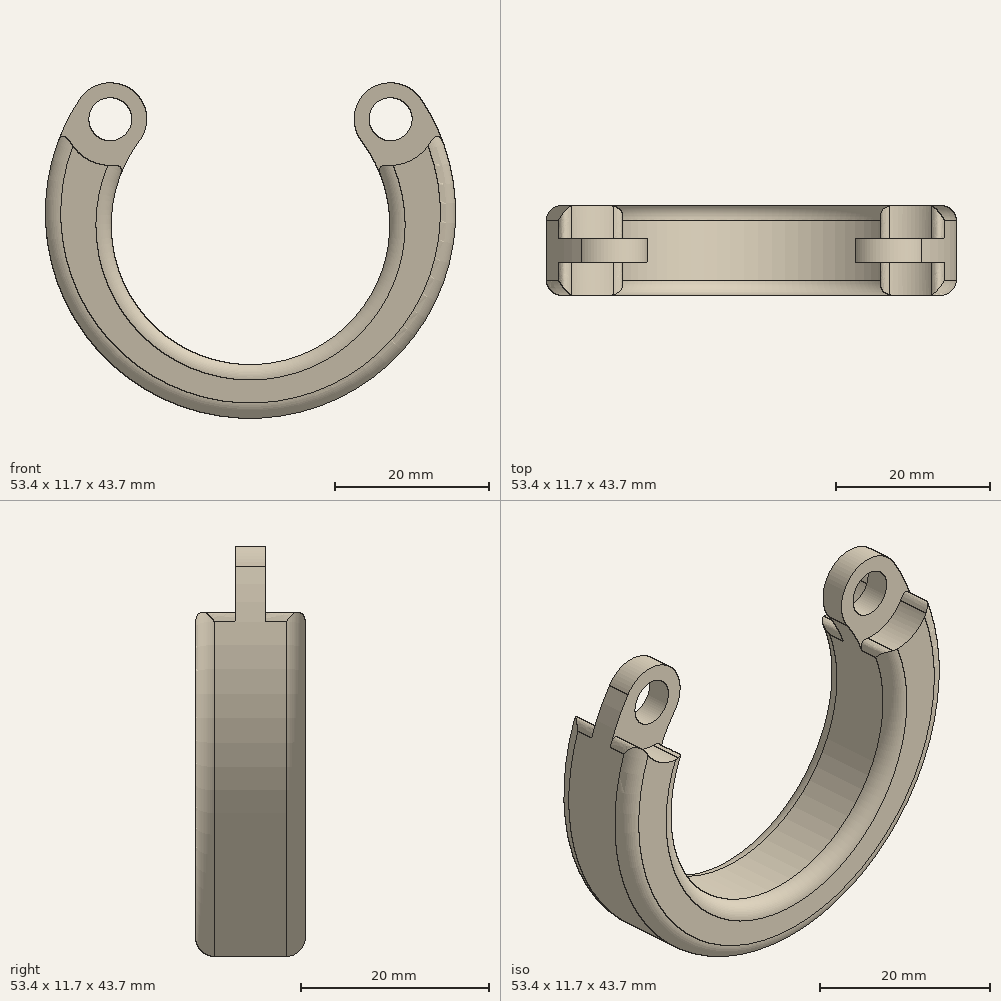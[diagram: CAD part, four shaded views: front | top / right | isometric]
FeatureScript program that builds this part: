
annotation { "Feature Type Name" : "Feature", "Feature Type Description" : "" }
export const myFeature = defineFeature(function(context is Context, id is Id, definition is map)
    precondition{}
    {
        {
            var Q0;
            Q0=qCreatedBy(makeId("Front.planeOp"),FACE);
            var sketch = newSketch(context, id + "F0", { "sketchPlane" : qUnion([Q0])});
            skLineSegment(sketch, "E0", {"start": v(-40.89, 0) * mm, "end": v(37.52, 0) * mm, "construction": true});
            skLineSegment(sketch, "E1", {"start": v(0, 27.57) * mm, "end": v(0, -28.48) * mm});
            skLineSegment(sketch, "E2", {"start": v(-18.25, 13.03) * mm, "end": v(18.25, 13.03) * mm, "construction": true});
            skCircle(sketch, "E3", {"center": v(0, 0) * mm, "radius": 22.42 * mm, "construction": true});
            skCircle(sketch, "E4", {"center": v(-18.25, 13.03) * mm, "radius": 2.8 * mm});
            skCircle(sketch, "E5", {"center": v(18.25, 13.03) * mm, "radius": 2.8 * mm});
            skArc(sketch, "E6", {"start": v(-14.46, 10.16) * mm, "mid": v(0, -18.92) * mm, "end": v(14.46, 10.16) * mm});
            skArc(sketch, "E7", {"start": v(-22.2, 15.67) * mm, "mid": v(0, -25.92) * mm, "end": v(22.2, 15.67) * mm});
            skCircle(sketch, "E8", {"center": v(0, -22.42) * mm, "radius": 3.5 * mm, "construction": true});
            skLineSegment(sketch, "E9", {"start": v(-26.72, 20.07) * mm, "end": v(-26.72, -16.74) * mm, "construction": true});
            skLineSegment(sketch, "E10", {"start": v(26.72, 16.32) * mm, "end": v(26.72, -20.9) * mm, "construction": true});
            skLineSegment(sketch, "E11", {"start": v(33.4, 17.78) * mm, "end": v(-37.63, 17.78) * mm, "construction": true});
            skLineSegment(sketch, "E12", {"start": v(-22.93, -25.92) * mm, "end": v(22.17, -25.92) * mm, "construction": true});
            skArc(sketch, "E13.converted", {"start": v(-14.46, 10.16) * mm, "mid": v(-15.5, 16.9) * mm, "end": v(-22.2, 15.67) * mm});
            skArc(sketch, "E14.converted", {"start": v(22.2, 15.67) * mm, "mid": v(15.5, 16.9) * mm, "end": v(14.46, 10.16) * mm});
            skArc(sketch, "E15", {"start": v(16.19, 7.4) * mm, "mid": v(21.32, 7.87) * mm, "end": v(24.19, 12.15) * mm});
            skArc(sketch, "E16.trimOffspring", {"start": v(-24.19, 12.15) * mm, "mid": v(-21.32, 7.87) * mm, "end": v(-16.19, 7.4) * mm});
            skSolve(sketch);
        }
        {
            var Q0;
            Q0=makeQuery(id+"F0.imprint","IMPRINT",FACE,{"disambiguationData":[TD([[makeQuery(id+"F0.imprint","IMPRINT",EDGE,{"derivedFrom":sQuery(id+"F0.wireOp",EDGE,"E4")}),-1.0]])]});
            var Q1;
            Q1=makeQuery(id+"F0.imprint","IMPRINT",FACE,{"disambiguationData":[TD([[makeQuery(id+"F0.imprint","IMPRINT",EDGE,{"derivedFrom":sQuery(id+"F0.wireOp",EDGE,"E5")}),-1.0]])]});
            extrude(context, id + "F1", {"entities" : qUnion([Q0, Q1]), "endBound" : BoundingType.SYMMETRIC, "depth" : 3.1 * mm, "offsetDistance" : 25 * mm});
        }
        {
            var Q0;
            {var subQ5=sQuery(id+"F0.wireOp",EDGE,"E15");Q0=makeQuery(id+"F0.imprint","IMPRINT",FACE,{"disambiguationData":[TD([[makeQuery(id+"F0.imprint","IMPRINT",EDGE,{"derivedFrom":subQ5}),-1.0]])]});}
            var Q1;
            {var subQ5=sQuery(id+"F0.wireOp",EDGE,"E16.trimOffspring");Q1=makeQuery(id+"F0.imprint","IMPRINT",FACE,{"disambiguationData":[TD([[makeQuery(id+"F0.imprint","IMPRINT",EDGE,{"derivedFrom":subQ5}),-1.0]])]});}
            extrude(context, id + "F2", {"entities" : qUnion([Q0, Q1]), "operationType" : NewBodyOperationType.ADD, "endBound" : BoundingType.SYMMETRIC, "depth" : 11.7 * mm, "offsetDistance" : 25 * mm});
        }
        {
            var Q0;
            {var subQ0=sQuery(id+"F0.wireOp",EDGE,"E7");var subQ1=makeQuery(id+"F2.opExtrude","SWEPT_FACE",FACE,{"disambiguationData":[OSD([subQ0])]});var subQ2=sQuery(id+"F0.wireOp",EDGE,"E13.converted");var subQ3=makeQuery(id+"F2.opExtrude","SWEPT_FACE",FACE,{"disambiguationData":[OSD([subQ2])]});Q0=makeQuery(id+"F2.boolean.opBoolean","SPLIT",EDGE,{"disambiguationData":[topologyDisambiguationEdgeConnected([subQ1,subQ3]),TD([makeQuery(id+"F1.opExtrude","CAP_FACE",FACE,{"disambiguationData":[OSD([sQuery(id+"F0.wireOp",EDGE,"E4"),subQ2])],"isStart":true})])],"derivedFrom":makeQuery(id+"F2.opExtrude","SWEPT_EDGE",EDGE,{"disambiguationData":[OSD([subQ0,subQ2])]})});}
            var Q1;
            {var subQ0=sQuery(id+"F0.wireOp",EDGE,"E7");var subQ1=makeQuery(id+"F2.opExtrude","SWEPT_FACE",FACE,{"disambiguationData":[OSD([subQ0])]});var subQ2=sQuery(id+"F0.wireOp",EDGE,"E13.converted");var subQ3=makeQuery(id+"F2.opExtrude","SWEPT_FACE",FACE,{"disambiguationData":[OSD([subQ2])]});Q1=makeQuery(id+"F2.boolean.opBoolean","SPLIT",EDGE,{"disambiguationData":[topologyDisambiguationEdgeConnected([subQ1,subQ3]),TD([makeQuery(id+"F1.opExtrude","CAP_FACE",FACE,{"disambiguationData":[OSD([sQuery(id+"F0.wireOp",EDGE,"E4"),subQ2])],"isStart":false})])],"derivedFrom":makeQuery(id+"F2.opExtrude","SWEPT_EDGE",EDGE,{"disambiguationData":[OSD([subQ0,subQ2])]})});}
            var Q2;
            {var subQ0=sQuery(id+"F0.wireOp",EDGE,"E13.converted");var subQ1=sQuery(id+"F0.wireOp",EDGE,"E6");var subQ2=makeQuery(id+"F2.opExtrude","SWEPT_FACE",FACE,{"disambiguationData":[OSD([subQ1])]});var subQ3=makeQuery(id+"F2.opExtrude","SWEPT_FACE",FACE,{"disambiguationData":[OSD([subQ0])]});Q2=makeQuery(id+"F2.boolean.opBoolean","SPLIT",EDGE,{"disambiguationData":[topologyDisambiguationEdgeConnected([subQ2,subQ3]),TD([makeQuery(id+"F1.opExtrude","CAP_FACE",FACE,{"disambiguationData":[OSD([sQuery(id+"F0.wireOp",EDGE,"E4"),subQ0])],"isStart":false})])],"derivedFrom":makeQuery(id+"F2.opExtrude","SWEPT_EDGE",EDGE,{"disambiguationData":[OSD([subQ1,subQ0])]})});}
            var Q3;
            {var subQ0=sQuery(id+"F0.wireOp",EDGE,"E13.converted");var subQ1=sQuery(id+"F0.wireOp",EDGE,"E6");var subQ2=makeQuery(id+"F2.opExtrude","SWEPT_FACE",FACE,{"disambiguationData":[OSD([subQ1])]});var subQ3=makeQuery(id+"F2.opExtrude","SWEPT_FACE",FACE,{"disambiguationData":[OSD([subQ0])]});Q3=makeQuery(id+"F2.boolean.opBoolean","SPLIT",EDGE,{"disambiguationData":[topologyDisambiguationEdgeConnected([subQ2,subQ3]),TD([makeQuery(id+"F1.opExtrude","CAP_FACE",FACE,{"disambiguationData":[OSD([sQuery(id+"F0.wireOp",EDGE,"E4"),subQ0])],"isStart":true})])],"derivedFrom":makeQuery(id+"F2.opExtrude","SWEPT_EDGE",EDGE,{"disambiguationData":[OSD([subQ1,subQ0])]})});}
            var Q4;
            {var subQ0=sQuery(id+"F0.wireOp",EDGE,"E14.converted");var subQ1=sQuery(id+"F0.wireOp",EDGE,"E6");var subQ2=makeQuery(id+"F2.opExtrude","SWEPT_FACE",FACE,{"disambiguationData":[OSD([subQ1])]});var subQ3=makeQuery(id+"F2.opExtrude","SWEPT_FACE",FACE,{"disambiguationData":[OSD([subQ0])]});Q4=makeQuery(id+"F2.boolean.opBoolean","SPLIT",EDGE,{"disambiguationData":[topologyDisambiguationEdgeConnected([subQ2,subQ3]),TD([makeQuery(id+"F1.opExtrude","CAP_FACE",FACE,{"disambiguationData":[OSD([sQuery(id+"F0.wireOp",EDGE,"E5"),subQ0])],"isStart":false})])],"derivedFrom":makeQuery(id+"F2.opExtrude","SWEPT_EDGE",EDGE,{"disambiguationData":[OSD([subQ1,subQ0])]})});}
            var Q5;
            {var subQ0=sQuery(id+"F0.wireOp",EDGE,"E7");var subQ1=makeQuery(id+"F2.opExtrude","SWEPT_FACE",FACE,{"disambiguationData":[OSD([subQ0])]});var subQ2=sQuery(id+"F0.wireOp",EDGE,"E14.converted");var subQ3=makeQuery(id+"F2.opExtrude","SWEPT_FACE",FACE,{"disambiguationData":[OSD([subQ2])]});Q5=makeQuery(id+"F2.boolean.opBoolean","SPLIT",EDGE,{"disambiguationData":[topologyDisambiguationEdgeConnected([subQ1,subQ3]),TD([makeQuery(id+"F1.opExtrude","CAP_FACE",FACE,{"disambiguationData":[OSD([sQuery(id+"F0.wireOp",EDGE,"E5"),subQ2])],"isStart":false})])],"derivedFrom":makeQuery(id+"F2.opExtrude","SWEPT_EDGE",EDGE,{"disambiguationData":[OSD([subQ0,subQ2])]})});}
            var Q6;
            {var subQ0=sQuery(id+"F0.wireOp",EDGE,"E6");var subQ1=makeQuery(id+"F2.opExtrude","SWEPT_FACE",FACE,{"disambiguationData":[OSD([subQ0])]});var subQ2=sQuery(id+"F0.wireOp",EDGE,"E14.converted");var subQ3=makeQuery(id+"F2.opExtrude","SWEPT_FACE",FACE,{"disambiguationData":[OSD([subQ2])]});Q6=makeQuery(id+"F2.boolean.opBoolean","SPLIT",EDGE,{"disambiguationData":[topologyDisambiguationEdgeConnected([subQ1,subQ3]),TD([makeQuery(id+"F1.opExtrude","CAP_FACE",FACE,{"disambiguationData":[OSD([sQuery(id+"F0.wireOp",EDGE,"E5"),subQ2])],"isStart":true})])],"derivedFrom":makeQuery(id+"F2.opExtrude","SWEPT_EDGE",EDGE,{"disambiguationData":[OSD([subQ0,subQ2])]})});}
            var Q7;
            {var subQ0=sQuery(id+"F0.wireOp",EDGE,"E14.converted");var subQ1=sQuery(id+"F0.wireOp",EDGE,"E7");var subQ2=makeQuery(id+"F2.opExtrude","SWEPT_FACE",FACE,{"disambiguationData":[OSD([subQ1])]});var subQ3=makeQuery(id+"F2.opExtrude","SWEPT_FACE",FACE,{"disambiguationData":[OSD([subQ0])]});Q7=makeQuery(id+"F2.boolean.opBoolean","SPLIT",EDGE,{"disambiguationData":[topologyDisambiguationEdgeConnected([subQ2,subQ3]),TD([makeQuery(id+"F1.opExtrude","CAP_FACE",FACE,{"disambiguationData":[OSD([sQuery(id+"F0.wireOp",EDGE,"E5"),subQ0])],"isStart":true})])],"derivedFrom":makeQuery(id+"F2.opExtrude","SWEPT_EDGE",EDGE,{"disambiguationData":[OSD([subQ1,subQ0])]})});}
            fillet(context, id + "F3", {"entities" : qUnion([Q0, Q1, Q2, Q3, Q4, Q5, Q6, Q7]), "radius" : 1 * mm, "tangentPropagation" : true, "rho" : 0.5, "crossSection" : FilletCrossSection.CONIC, "allowEdgeOverflow" : false});
        }
        {
            var Q0;
            Q0=makeQuery(id+"F2.opExtrude","CAP_EDGE",EDGE,{"disambiguationData":[OSD([sQuery(id+"F0.wireOp",EDGE,"E6")])],"isStart":true});
            var Q1;
            Q1=makeQuery(id+"F2.opExtrude","CAP_EDGE",EDGE,{"disambiguationData":[OSD([sQuery(id+"F0.wireOp",EDGE,"E7")])],"isStart":true});
            var Q2;
            Q2=makeQuery(id+"F2.opExtrude","CAP_EDGE",EDGE,{"disambiguationData":[OSD([sQuery(id+"F0.wireOp",EDGE,"E7")])],"isStart":false});
            var Q3;
            Q3=makeQuery(id+"F2.opExtrude","CAP_EDGE",EDGE,{"disambiguationData":[OSD([sQuery(id+"F0.wireOp",EDGE,"E6")])],"isStart":false});
            fillet(context, id + "F4", {"entities" : qUnion([Q0, Q1, Q2, Q3]), "radius" : 2 * mm, "allowEdgeOverflow" : false});
        }
    });
